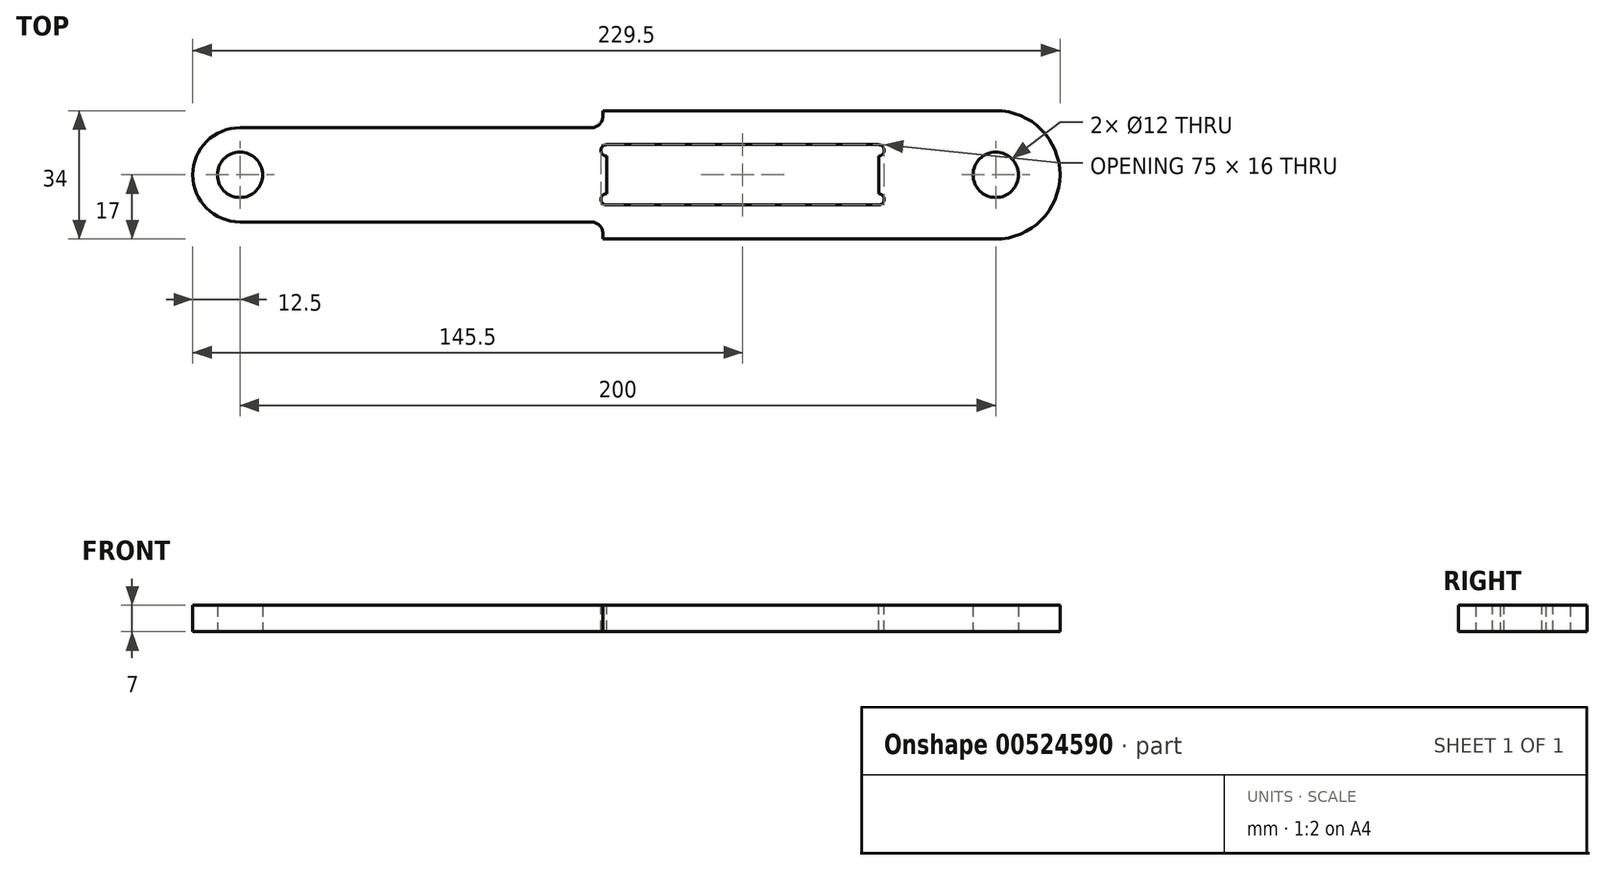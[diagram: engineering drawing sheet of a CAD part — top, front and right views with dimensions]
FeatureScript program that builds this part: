
annotation { "Feature Type Name" : "Feature", "Feature Type Description" : "" }
export const myFeature = defineFeature(function(context is Context, id is Id, definition is map)
    precondition{}
    {
        {
            var Q0;
            Q0=qCreatedBy(makeId("Top.planeOp"),FACE);
            var sketch = newSketch(context, id + "F0", { "sketchPlane" : qUnion([Q0])});
            skCircle(sketch, "E0", {"center": v(0, 0) * mm, "radius": 17 * mm});
            skCircle(sketch, "E1", {"center": v(0, 0) * mm, "radius": 6 * mm});
            skLineSegment(sketch, "E2", {"start": v(0, 0) * mm, "end": v(-200, 0) * mm, "construction": true});
            skCircle(sketch, "E3", {"center": v(-200, 0) * mm, "radius": 12.5 * mm});
            skCircle(sketch, "E4", {"center": v(-200, 0) * mm, "radius": 6 * mm});
            skLineSegment(sketch, "E5", {"start": v(-200, 12.5) * mm, "end": v(-104, 12.5) * mm});
            skLineSegment(sketch, "E6", {"start": v(-104, 12.5) * mm, "end": v(-104, 17) * mm});
            skLineSegment(sketch, "E7", {"start": v(-104, 17) * mm, "end": v(0, 17) * mm});
            skLineSegment(sketch, "E8.MirrorCS", {"start": v(-200, -12.5) * mm, "end": v(-104, -12.5) * mm});
            skLineSegment(sketch, "E9.MirrorCS", {"start": v(-104, -12.5) * mm, "end": v(-104, -17) * mm});
            skLineSegment(sketch, "E10.MirrorCS", {"start": v(-104, -17) * mm, "end": v(0, -17) * mm});
            skSolve(sketch);
        }
        {
            var Q0;
            {var subQ0=sQuery(id+"F0.wireOp",EDGE,"E5");Q0=makeQuery(id+"F0.imprint","IMPRINT",FACE,{"disambiguationData":[TD([[makeQuery(id+"F0.imprint","IMPRINT",EDGE,{"derivedFrom":subQ0}),-1.0]])]});}
            var Q1;
            Q1=makeQuery(id+"F0.imprint","IMPRINT",FACE,{"disambiguationData":[TD([[makeQuery(id+"F0.imprint","IMPRINT",EDGE,{"derivedFrom":sQuery(id+"F0.wireOp",EDGE,"E1")}),-1.0]])]});
            var Q2;
            Q2=makeQuery(id+"F0.imprint","IMPRINT",FACE,{"disambiguationData":[TD([[makeQuery(id+"F0.imprint","IMPRINT",EDGE,{"derivedFrom":sQuery(id+"F0.wireOp",EDGE,"E4")}),-1.0]])]});
            extrude(context, id + "F1", {"entities" : qUnion([Q0, Q1, Q2]), "depth" : 7 * mm, "offsetDistance" : 25 * mm});
        }
        {
            var Q0;
            Q0=makeQuery(id+"F1.opExtrude","CAP_FACE",FACE,{"disambiguationData":[OSD([sQuery(id+"F0.wireOp",EDGE,"E0"),sQuery(id+"F0.wireOp",EDGE,"E1"),sQuery(id+"F0.wireOp",EDGE,"E3"),sQuery(id+"F0.wireOp",EDGE,"E4"),sQuery(id+"F0.wireOp",EDGE,"E5"),sQuery(id+"F0.wireOp",EDGE,"E6"),sQuery(id+"F0.wireOp",EDGE,"E7"),sQuery(id+"F0.wireOp",EDGE,"E8.MirrorCS"),sQuery(id+"F0.wireOp",EDGE,"E9.MirrorCS"),sQuery(id+"F0.wireOp",EDGE,"E10.MirrorCS")])],"isStart":false});
            var sketch = newSketch(context, id + "F2", { "sketchPlane" : qUnion([Q0])});
            skLineSegment(sketch, "E11.bottom", {"start": v(-31, 8) * mm, "end": v(-103, 8) * mm});
            skLineSegment(sketch, "E11.top", {"start": v(-31, -8) * mm, "end": v(-103, -8) * mm});
            skLineSegment(sketch, "E11.left", {"start": v(-31, 8) * mm, "end": v(-31, -8) * mm});
            skLineSegment(sketch, "E11.right", {"start": v(-103, 8) * mm, "end": v(-103, -8) * mm});
            skPoint(sketch, "E11.middle", {"position": v(-67, 0) * mm});
            skCircle(sketch, "E12", {"center": v(-31, 6.5) * mm, "radius": 1.5 * mm});
            skCircle(sketch, "E13", {"center": v(-31, -6.5) * mm, "radius": 1.5 * mm});
            skCircle(sketch, "E14", {"center": v(-103, 6.5) * mm, "radius": 1.5 * mm});
            skCircle(sketch, "E15", {"center": v(-103, -6.5) * mm, "radius": 1.5 * mm});
            skSolve(sketch);
        }
        {
            var Q0;
            Q0 = qSketchRegion(id + "F2", true);
            extrude(context, id + "F3", {"entities" : qUnion([Q0]), "operationType" : NewBodyOperationType.REMOVE, "endBound" : BoundingType.THROUGH_ALL, "oppositeDirection" : true, "depth" : 25 * mm, "offsetDistance" : 25 * mm});
        }
        {
            var Q0;
            Q0=makeQuery(id+"F1.opExtrude","SWEPT_EDGE",EDGE,{"disambiguationData":[OSD([sQuery(id+"F0.wireOp",EDGE,"E5"),sQuery(id+"F0.wireOp",EDGE,"E6")])]});
            var Q1;
            Q1=makeQuery(id+"F1.opExtrude","SWEPT_EDGE",EDGE,{"disambiguationData":[OSD([sQuery(id+"F0.wireOp",EDGE,"E8.MirrorCS"),sQuery(id+"F0.wireOp",EDGE,"E9.MirrorCS")])]});
            fillet(context, id + "F4", {"entities" : qUnion([Q0, Q1]), "radius" : 3 * mm, "tangentPropagation" : true, "allowEdgeOverflow" : false});
        }
    });
